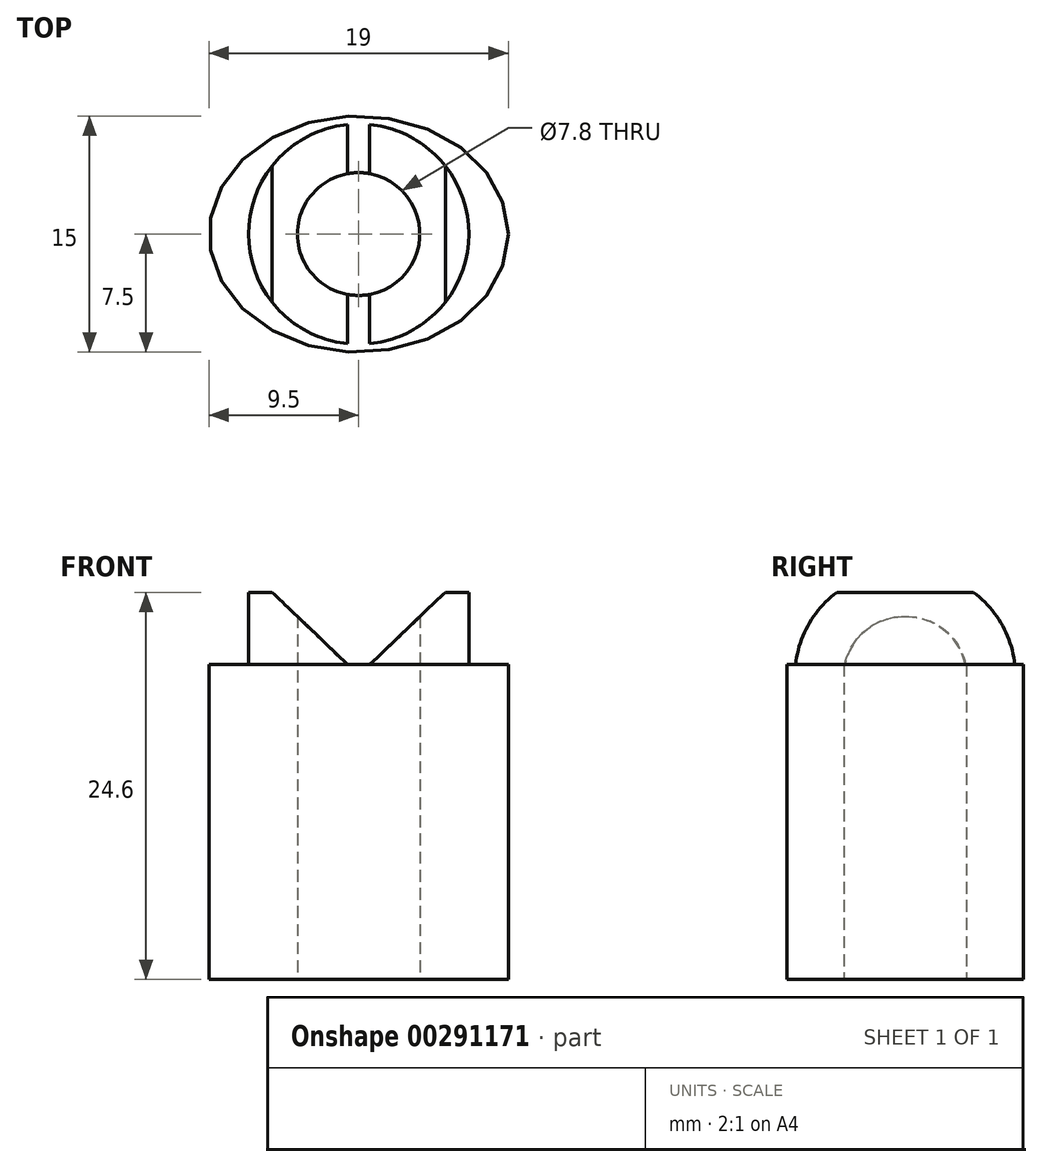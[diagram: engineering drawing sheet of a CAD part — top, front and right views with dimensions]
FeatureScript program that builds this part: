
annotation { "Feature Type Name" : "Feature", "Feature Type Description" : "" }
export const myFeature = defineFeature(function(context is Context, id is Id, definition is map)
    precondition{}
    {
        {
            var Q0;
            Q0=qCreatedBy(makeId("Top.planeOp"),FACE);
            var sketch = newSketch(context, id + "F0", { "sketchPlane" : qUnion([Q0])});
            skEllipse(sketch, "E0", {"center": v(0, 0) * mm, "majorRadius": 9.5 * mm, "minorRadius": 7.5 * mm, "majorAxis": v(1, 0)});
            skSolve(sketch);
        }
        {
            var Q0;
            Q0=makeQuery(id+"F0.imprint","IMPRINT",FACE,{"disambiguationData":[TD([[makeQuery(id+"F0.imprint","IMPRINT",EDGE,{"derivedFrom":sQuery(id+"F0.wireOp",EDGE,"E0")}),1.0]])]});
            extrude(context, id + "F1", {"entities" : qUnion([Q0]), "depth" : 20 * mm});
        }
        {
            var Q0;
            Q0=makeQuery(id+"F1.opExtrude","CAP_FACE",FACE,{"disambiguationData":[OSD([sQuery(id+"F0.wireOp",EDGE,"E0")])],"isStart":false});
            var sketch = newSketch(context, id + "F2", { "sketchPlane" : qUnion([Q0])});
            skCircle(sketch, "E1", {"center": v(0, 0) * mm, "radius": 7 * mm});
            skSolve(sketch);
        }
        {
            var Q0;
            Q0=makeQuery(id+"F2.imprint","IMPRINT",FACE,{"disambiguationData":[TD([[makeQuery(id+"F2.imprint","IMPRINT",EDGE,{"derivedFrom":sQuery(id+"F2.wireOp",EDGE,"E1")}),1.0]])]});
            extrude(context, id + "F3", {"entities" : qUnion([Q0]), "operationType" : NewBodyOperationType.ADD, "depth" : 4.6 * mm});
        }
        {
            var Q0;
            Q0=qCreatedBy(makeId("Front.planeOp"),FACE);
            var sketch = newSketch(context, id + "F4", { "sketchPlane" : qUnion([Q0])});
            skLineSegment(sketch, "E2.bottom", {"start": v(-0.7, 20) * mm, "end": v(0.7, 20) * mm});
            skLineSegment(sketch, "E2.top", {"start": v(-0.7, 24.6) * mm, "end": v(0.7, 24.6) * mm});
            skLineSegment(sketch, "E3.top", {"start": v(-5.5, 24.6) * mm, "end": v(5.5, 24.6) * mm});
            skLineSegment(sketch, "E4", {"start": v(-0.7, 20) * mm, "end": v(-5.5, 24.6) * mm});
            skLineSegment(sketch, "E5", {"start": v(5.5, 24.6) * mm, "end": v(0.7, 20) * mm});
            skSolve(sketch);
        }
        {
            var Q0;
            Q0=qSketchRegion(id+"F4",true);
            extrude(context, id + "F5", {"entities" : qUnion([Q0]), "operationType" : NewBodyOperationType.REMOVE, "depth" : 25 * mm, "symmetric" : true});
        }
        {
            var Q0;
            Q0=makeQuery(id+"F1.opExtrude","CAP_FACE",FACE,{"disambiguationData":[OSD([sQuery(id+"F0.wireOp",EDGE,"E0")])],"isStart":true});
            var sketch = newSketch(context, id + "F6", { "sketchPlane" : qUnion([Q0])});
            skCircle(sketch, "E6", {"center": v(0, 0) * mm, "radius": 3.9 * mm});
            skSolve(sketch);
        }
        {
            var Q0;
            Q0=qSketchRegion(id+"F6",true);
            extrude(context, id + "F7", {"entities" : qUnion([Q0]), "operationType" : NewBodyOperationType.REMOVE, "endBound" : BoundingType.THROUGH_ALL, "oppositeDirection" : true, "depth" : 25 * mm});
        }
    });
